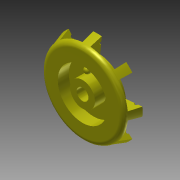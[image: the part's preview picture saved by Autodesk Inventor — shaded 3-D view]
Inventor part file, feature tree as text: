
AUTODESK INVENTOR PART (.ipt)
format: ipt  version: 2014 (Build 180170000, 170)  size: 267,264 bytes
history: native  units: in
note: dims shown in document units (in); Inventor stores cm internally (conversion verified against a paired STEP export)
features: sketch x10, extrude x7, fillet x2, pattern_circular x2, plane x1, loft x1, revolve x1, projected_geometry x1
ambient origin geometry x8: Origin, YZ Plane, XZ Plane, XY Plane, X Axis, Y Axis, Z Axis, Center Point
bodies: Solid1 (feature_tree)
feature tree (25):
  extrude  "Extrusion1"  Depth=0.083in
  fillet  "Fillet1"  Radius=0.11in
  extrude  "Extrusion2"  Depth=0.083in TaperAngle=0.0deg
  extrude  "Extrusion3"  Depth=0.2395in TaperAngle=0.0deg
  plane  "Work Plane1"
  extrude  "Extrusion5"  Depth=0.083in TaperAngle=0.0deg
  extrude  "Extrusion6"  Depth=0.254in
  extrude  "Extrusion7"  Depth=0.083in TaperAngle=0.0deg
  extrude  "Extrusion8"  Depth=0.191in
  fillet  "Fillet2"  Radius=0.191in
  loft  "Loft2"
  pattern_circular  "Circular Pattern1"  Angle=90.0deg  [1 undecoded]
  revolve  "Revolution1"  Angle=90.0deg
  pattern_circular  "Circular Pattern2"  Count=8 Angle=360.0deg
  sketch  "Sketch1"  dims[d0=1.793in d1=0.083in d2=-0.1031in d3=0.11in]
  sketch  "Sketch2"  dims[d4=1.068in d5=0.083in d6=0.0in]
  sketch  "Sketch3"  dims[d7=0.083in d8=0.2395in d9=0.0in]
  sketch  "Sketch5"  dims[d12=-0.238in d13=0.083in d14=0.0in]
  projected_geometry  "Projected Loop1"
  sketch  "Sketch6"  dims[d15=0.538in d16=0.254in]
  sketch  "Sketch7"  dims[d17=0.083in d18=0.0in d19=0.083in d20=0.0in]
  sketch  "Sketch8"  dims[d21=0.136in d22=0.063in d23=0.191in d24=0.0in]
  sketch  "Sketch11"  dims[d25=0.06in d35=0.172in]
  sketch  "Sketch12"  dims[d36=0.086in]
  sketch  "Sketch13"  dims[d38=0.975in d39=0.0in d40=90.0deg d41=0.0in d42=90.0deg d43=3.1496in d44=360.0deg d46=45.0deg d47=67.5deg d48=67.5deg d49=0.032in d50=0.04in d51=0.04in d52=0.093in d53=90.0deg d54=3.1496in d55=360.0deg d57=0.5823in]
note: 1 required parameter value undecoded (feature->parameter linkage not recoverable at this tier; creation-order binding heuristic only, values carry confidence <= 0.55)
